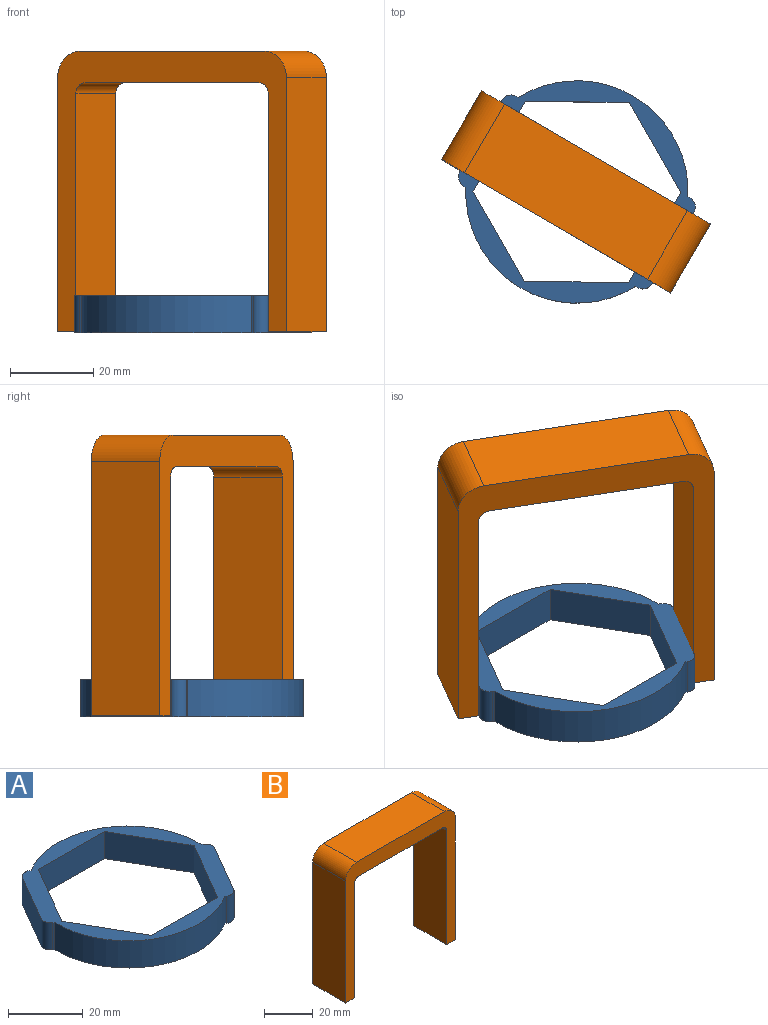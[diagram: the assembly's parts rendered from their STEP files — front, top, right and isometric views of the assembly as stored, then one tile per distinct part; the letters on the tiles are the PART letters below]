
ASSEMBLY  parts=2 mates=1
PART A: 20 faces, bbox 56.8x53.3x8.9 mm
  f0: cylinder r=26.67mm len=40.77mm, axis (0,0,-1), area 514.2mm2, adj f8,f9,f10,f13
  f1: cylinder r=26.67mm len=40.77mm, axis (0,0,-1), area 514.2mm2, adj f8,f9,f12,f15
  f2: plane 21.64x12.38mm, normal (-0.87,-0.5,0), area 221.6mm2, adj f3,f7,f8,f9
  f3: plane 21.54x12.55mm, normal (-0.86,0.5,0), area 221.6mm2, adj f2,f4,f8,f9
  f4: plane 24.93x8.89mm, normal (0,1,0), area 221.6mm2, adj f3,f5,f8,f9
  f5: plane 21.64x12.38mm, normal (0.87,0.5,0), area 221.6mm2, adj f4,f6,f8,f9
  f6: plane 21.54x12.55mm, normal (0.86,-0.5,0), area 221.6mm2, adj f5,f7,f8,f9
  f7: plane 24.93x8.89mm, normal (0,-1,0), area 221.6mm2, adj f2,f6,f8,f9
  f8: plane 56.77x53.34mm, normal (0,0,1), area 664.5mm2, adj f0,f1,f2,f3,f4,f5,f6,f7
  f9: plane 56.77x53.34mm, normal (0,0,-1), area 664.5mm2, adj f0,f1,f2,f3,f4,f5,f6,f7
  f10: plane 8.89x0.48mm, normal (0.5,0.86,0), area 4.9mm2, adj f0,f8,f9,f18
  f11: plane 17.15x9.99mm, normal (-0.86,0.5,0), area 176.5mm2, adj f8,f9,f18,f19
  f12: plane 8.89x0.48mm, normal (-0.5,-0.86,0), area 4.9mm2, adj f1,f8,f9,f19
  f13: plane 8.89x0.48mm, normal (0.5,0.86,0), area 4.9mm2, adj f0,f8,f9,f17
  f14: plane 17.15x9.99mm, normal (0.86,-0.5,0), area 176.5mm2, adj f8,f9,f16,f17
  f15: plane 8.89x0.48mm, normal (-0.5,-0.86,0), area 4.9mm2, adj f1,f8,f9,f16
  f16: cylinder r=2.54mm len=8.89mm, axis (0,0,1), area 35.5mm2, adj f8,f9,f14,f15
  f17: cylinder r=2.54mm len=8.89mm, axis (0,0,1), area 35.5mm2, adj f8,f9,f13,f14
  f18: cylinder r=2.54mm len=8.89mm, axis (0,0,1), area 35.5mm2, adj f8,f9,f10,f11
  f19: cylinder r=2.54mm len=8.89mm, axis (0,0,1), area 35.5mm2, adj f8,f9,f11,f12
PART B: 14 faces, bbox 63.5x19.1x67.3 mm
  f0: plane 60.96x19.05mm, normal (-1,0,0), area 1161.3mm2, adj f1,f8,f9,f11
  f1: plane 19.05x5.08mm, normal (0,0,-1), area 96.8mm2, adj f0,f2,f8,f9
  f2: plane 57.15x19.05mm, normal (1,0,0), area 1088.7mm2, adj f1,f8,f9,f12
  f3: plane 48.26x19.05mm, normal (0,0,-1), area 919.4mm2, adj f8,f9,f12,f13
  f4: plane 57.15x19.05mm, normal (-1,0,0), area 1088.7mm2, adj f5,f8,f9,f13
  f5: plane 19.05x5.08mm, normal (0,0,-1), area 96.8mm2, adj f4,f6,f8,f9
  f6: plane 60.96x19.05mm, normal (1,0,0), area 1161.3mm2, adj f5,f8,f9,f10
  f7: plane 50.8x19.05mm, normal (0,0,1), area 967.7mm2, adj f8,f9,f10,f11
  f8: plane 67.31x63.5mm, normal (0,-1,0), area 1075.8mm2, adj f0,f1,f2,f3,f4,f5,f6,f7
  f9: plane 67.31x63.5mm, normal (0,1,0), area 1075.8mm2, adj f0,f1,f2,f3,f4,f5,f6,f7
  f10: cylinder r=6.35mm len=19.05mm, axis (0,1,0), area 190mm2, adj f6,f7,f8,f9
  f11: cylinder r=6.35mm len=19.05mm, axis (0,1,0), area 190mm2, adj f0,f7,f8,f9
  f12: cylinder r=2.54mm len=19.05mm, axis (0,-1,0), area 76mm2, adj f2,f3,f8,f9
  f13: cylinder r=2.54mm len=19.05mm, axis (0,-1,0), area 76mm2, adj f3,f4,f8,f9
PLACE A t=(-1.62,-1.16,-4.78)mm fixed
PLACE B rot(axis=(0,0,-1),30.2deg) t=(-24.47,23.03,-4.49)mm
MATE parallel B.f2 <-> A.f11  axis (0.86,-0.5,0) through (-24.87,12.24,-4.49)mm
